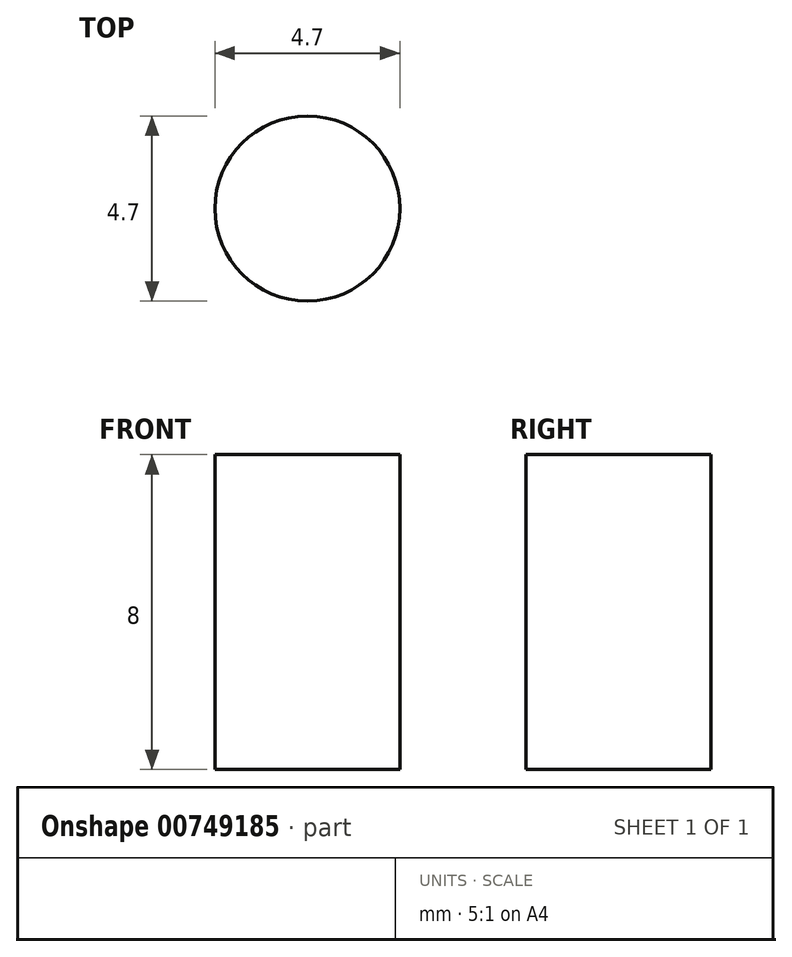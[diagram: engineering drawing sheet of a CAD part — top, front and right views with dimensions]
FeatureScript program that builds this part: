
annotation { "Feature Type Name" : "Feature", "Feature Type Description" : "" }
export const myFeature = defineFeature(function(context is Context, id is Id, definition is map)
    precondition{}
    {
        {
            var Q0;
            Q0=qCreatedBy(makeId("Top.planeOp"),FACE);
            var sketch = newSketch(context, id + "F0", { "sketchPlane" : qUnion([Q0])});
            skCircle(sketch, "E0", {"center": v(0, 0) * mm, "radius": 2.35 * mm});
            skSolve(sketch);
        }
        {
            var Q0;
            Q0=qSketchRegion(id+"F0",true);
            extrude(context, id + "F1", {"entities" : qUnion([Q0]), "depth" : 8 * mm, "offsetDistance" : 25 * mm});
        }
    });
